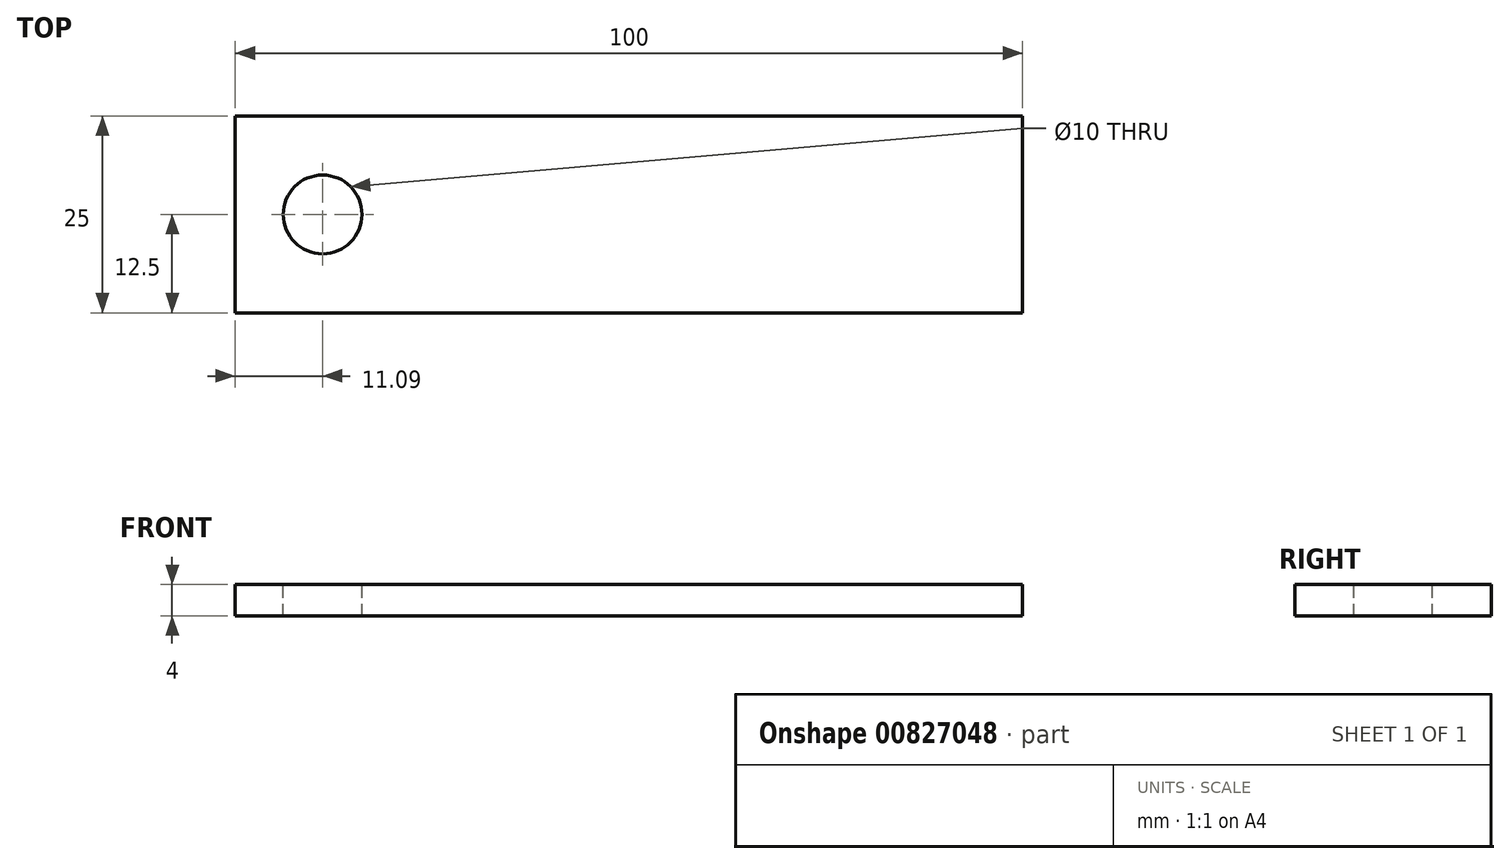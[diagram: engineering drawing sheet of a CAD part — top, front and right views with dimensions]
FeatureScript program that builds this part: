
annotation { "Feature Type Name" : "Feature", "Feature Type Description" : "" }
export const myFeature = defineFeature(function(context is Context, id is Id, definition is map)
    precondition{}
    {
        {
            var Q0;
            Q0=qCreatedBy(makeId("Front.planeOp"),FACE);
            var sketch = newSketch(context, id + "F0", { "sketchPlane" : qUnion([Q0])});
            skLineSegment(sketch, "E0.bottom", {"start": v(-6.09, 4) * mm, "end": v(93.91, 4) * mm});
            skLineSegment(sketch, "E0.top", {"start": v(-6.09, 0) * mm, "end": v(93.91, 0) * mm});
            skLineSegment(sketch, "E0.left", {"start": v(-6.09, 4) * mm, "end": v(-6.09, 0) * mm});
            skLineSegment(sketch, "E0.right", {"start": v(93.91, 4) * mm, "end": v(93.91, 0) * mm});
            skSolve(sketch);
        }
        {
            var Q0;
            Q0 = qSketchRegion(id + "F0", true);
            extrude(context, id + "F1", {"entities" : qUnion([Q0]), "endBound" : BoundingType.SYMMETRIC, "depth" : 25 * mm, "offsetDistance" : 25 * mm});
        }
        {
            var Q0;
            Q0=makeQuery(id+"F1.opExtrude","SWEPT_FACE",FACE,{"disambiguationData":[OSD([sQuery(id+"F0.wireOp",EDGE,"E0.bottom")])]});
            var sketch = newSketch(context, id + "F2", { "sketchPlane" : qUnion([Q0])});
            skPoint(sketch, "E1", {"position": v(5, 0) * mm});
            skSolve(sketch);
        }
        {
            var Q0;
            Q0=sQuery(id+"F2.wireOp",VERTEX,"E1");
            var Q1;
            Q1=makeQuery(id+"F1.opExtrude","SWEPT_BODY",BODY,{"disambiguationData":[OSD([sQuery(id+"F0.wireOp",EDGE,"E0.bottom"),sQuery(id+"F0.wireOp",EDGE,"E0.top"),sQuery(id+"F0.wireOp",EDGE,"E0.left"),sQuery(id+"F0.wireOp",EDGE,"E0.right")])]});
            hole(context, id + "F3", {"style" : HoleStyle.SIMPLE, "endStyle" : HoleEndStyle.THROUGH, "holeDiameter" : 10 * mm, "majorDiameter" : 5 * mm, "isTappedThrough" : true, "tappedDepth" : 12 * mm, "tapClearance" : 3, "locations" : qUnion([Q0]), "scope" : qUnion([Q1])});
        }
    });
